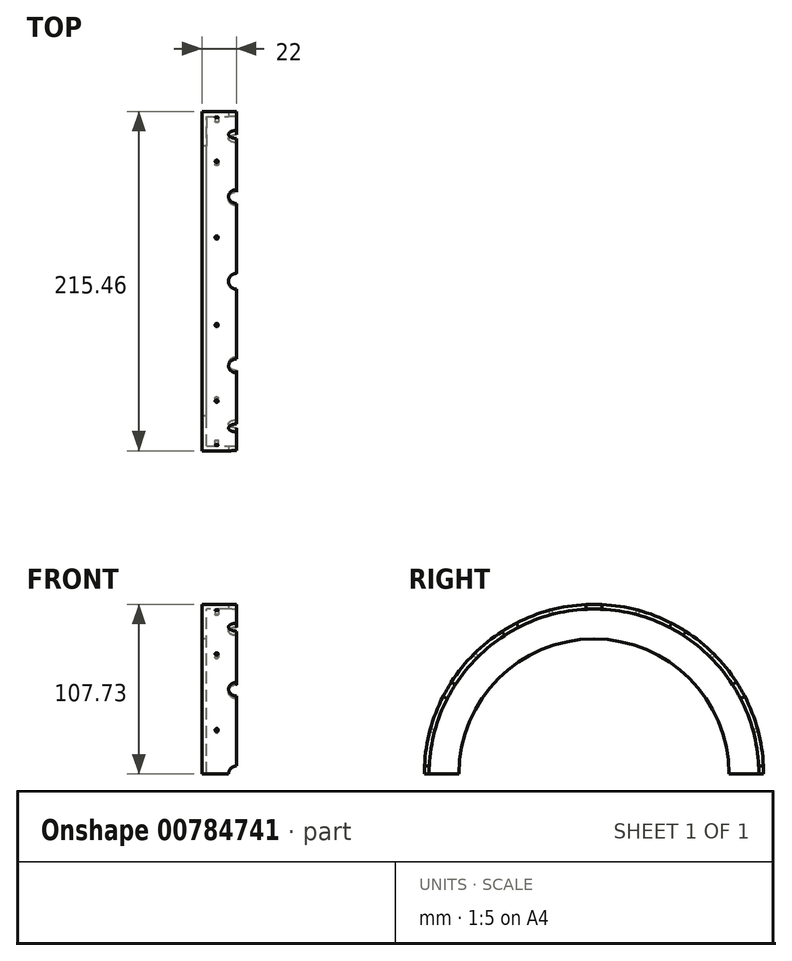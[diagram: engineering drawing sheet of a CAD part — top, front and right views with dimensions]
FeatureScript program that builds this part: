
annotation { "Feature Type Name" : "Feature", "Feature Type Description" : "" }
export const myFeature = defineFeature(function(context is Context, id is Id, definition is map)
    precondition{}
    {
        {
            var Q0;
            Q0=qCreatedBy(makeId("Top.planeOp"),FACE);
            var sketch = newSketch(context, id + "F0", { "sketchPlane" : qUnion([Q0])});
            skLineSegment(sketch, "E0", {"start": v(-37.45, 0) * mm, "end": v(31.85, 0) * mm, "construction": true});
            skLineSegment(sketch, "E1", {"start": v(-6.93, 104.73) * mm, "end": v(-6.93, 85.73) * mm});
            skLineSegment(sketch, "E2", {"start": v(-6.93, 85.73) * mm, "end": v(-9.93, 85.73) * mm});
            skLineSegment(sketch, "E3", {"start": v(-9.93, 85.73) * mm, "end": v(-9.93, 107.73) * mm});
            skLineSegment(sketch, "E4", {"start": v(-6.93, 104.73) * mm, "end": v(9.07, 104.73) * mm});
            skLineSegment(sketch, "E5", {"start": v(12.07, 107.73) * mm, "end": v(12.07, 104.73) * mm});
            skLineSegment(sketch, "E6", {"start": v(-9.93, 107.73) * mm, "end": v(12.07, 107.73) * mm});
            skLineSegment(sketch, "E7.trimOffspring", {"start": v(10.07, 104.73) * mm, "end": v(12.07, 104.73) * mm});
            skLineSegment(sketch, "E8", {"start": v(9.07, 104.73) * mm, "end": v(10.07, 104.73) * mm});
            skSolve(sketch);
        }
        {
            var Q0;
            Q0 = qSketchRegion(id + "F0", true);
            var Q1;
            Q1=sQuery(id+"F0.wireOp",EDGE,"E0");
            revolve(context, id + "F1", {"surfaceOperationType" : NewSurfaceOperationType.NEW, "entities" : qUnion([Q0]), "axis" : qUnion([Q1]), "revolveType" : RevolveType.ONE_DIRECTION, "angle" : 180 * degree});
        }
        {
            var Q0;
            Q0=qCreatedBy(makeId("Right.planeOp"),FACE);
            var sketch = newSketch(context, id + "F2", { "sketchPlane" : qUnion([Q0])});
            skLineSegment(sketch, "E9", {"start": v(0, 0) * mm, "end": v(61.84, 107.11) * mm, "construction": true});
            skLineSegment(sketch, "E10", {"start": v(0, 0) * mm, "end": v(0, 110.2) * mm, "construction": true});
            skLineSegment(sketch, "E11", {"start": v(0, 0) * mm, "end": v(-59.27, 102.65) * mm, "construction": true});
            skLineSegment(sketch, "E12", {"start": v(0, 0) * mm, "end": v(108.53, 62.66) * mm, "construction": true});
            skLineSegment(sketch, "E13", {"start": v(0, 0) * mm, "end": v(-111.98, 64.65) * mm, "construction": true});
            skLineSegment(sketch, "E14", {"start": v(0, 0) * mm, "end": v(-132.1, 0) * mm, "construction": true});
            skLineSegment(sketch, "E15", {"start": v(0, 0) * mm, "end": v(126.53, 0) * mm, "construction": true});
            skPoint(sketch, "E16", {"position": v(-59.27, 102.65) * mm});
            skPoint(sketch, "E17", {"position": v(-111.98, 64.65) * mm});
            skPoint(sketch, "E18", {"position": v(-132.1, 0) * mm});
            skPoint(sketch, "E19", {"position": v(0, 110.2) * mm});
            skPoint(sketch, "E20", {"position": v(61.84, 107.11) * mm});
            skPoint(sketch, "E21", {"position": v(108.53, 62.66) * mm});
            skPoint(sketch, "E22", {"position": v(126.53, 0) * mm});
            skLineSegment(sketch, "E23", {"start": v(0, 0) * mm, "end": v(-120.74, 32.35) * mm, "construction": true});
            skLineSegment(sketch, "E24.MirrorCS", {"start": v(0, 0) * mm, "end": v(-88.39, 88.39) * mm, "construction": true});
            skLineSegment(sketch, "E25.MirrorCS", {"start": v(0, 0) * mm, "end": v(-32.35, 120.74) * mm, "construction": true});
            skLineSegment(sketch, "E26.MirrorCS", {"start": v(0, 0) * mm, "end": v(32.35, 120.74) * mm, "construction": true});
            skLineSegment(sketch, "E27.MirrorCS", {"start": v(0, 0) * mm, "end": v(88.39, 88.39) * mm, "construction": true});
            skLineSegment(sketch, "E28.MirrorCS", {"start": v(0, 0) * mm, "end": v(120.74, 32.35) * mm, "construction": true});
            skSolve(sketch);
        }
        {
            var Q0;
            Q0=qCreatedBy(makeId("Front.planeOp"),FACE);
            var Q1;
            Q1=sQuery(id+"F2.wireOp",EDGE,"E13");
            cPlane(context, id + "F3", {"entities" : qUnion([Q0, Q1]), "cplaneType" : CPlaneType.LINE_ANGLE, "offset" : 25 * mm, "angle" : 0 * degree, "width" : 150 * mm, "height" : 150 * mm});
        }
        {
            var Q0;
            Q0=qCreatedBy(id+"F3.planeOp",FACE);
            var sketch = newSketch(context, id + "F4", { "sketchPlane" : qUnion([Q0])});
            skArc(sketch, "E29", {"start": v(12.07, -113.43) * mm, "mid": v(17.27, -105.94) * mm, "end": v(12.07, -98.44) * mm});
            skLineSegment(sketch, "E30", {"start": v(12.07, -113.43) * mm, "end": v(12.07, -98.44) * mm});
            skSolve(sketch);
        }
        {
            var Q0;
            Q0 = qSketchRegion(id + "F4", true);
            var Q1;
            Q1=sQuery(id+"F4.wireOp",EDGE,"E30");
            revolve(context, id + "F5", {"operationType" : NewBodyOperationType.REMOVE, "surfaceOperationType" : NewSurfaceOperationType.NEW, "entities" : qUnion([Q0]), "axis" : qUnion([Q1]), "revolveType" : RevolveType.FULL, "oppositeDirection" : true});
        }
        {
            var Q0;
            Q0=sQuery(id+"F2.wireOp",EDGE,"E11");
            cPlane(context, id + "F6", {"entities" : qUnion([Q0]), "cplaneType" : CPlaneType.LINE_ANGLE, "offset" : 25 * mm, "angle" : 90 * degree, "width" : 150 * mm, "height" : 150 * mm});
        }
        {
            var Q0;
            Q0=qCreatedBy(id+"F6.planeOp",FACE);
            var sketch = newSketch(context, id + "F7", { "sketchPlane" : qUnion([Q0])});
            skArc(sketch, "E31", {"start": v(-12.1, 98.77) * mm, "mid": v(-6.9, 106.26) * mm, "end": v(-12.1, 113.76) * mm});
            skLineSegment(sketch, "E32", {"start": v(-12.1, 98.77) * mm, "end": v(-12.1, 113.76) * mm});
            skSolve(sketch);
        }
        {
            var Q0;
            Q0 = qSketchRegion(id + "F7", true);
            var Q1;
            Q1=sQuery(id+"F7.wireOp",EDGE,"E32");
            revolve(context, id + "F8", {"operationType" : NewBodyOperationType.REMOVE, "surfaceOperationType" : NewSurfaceOperationType.NEW, "entities" : qUnion([Q0]), "axis" : qUnion([Q1]), "revolveType" : RevolveType.FULL, "oppositeDirection" : true});
        }
        {
            var Q0;
            Q0=sQuery(id+"F2.wireOp",EDGE,"E10");
            cPlane(context, id + "F9", {"entities" : qUnion([Q0]), "cplaneType" : CPlaneType.LINE_ANGLE, "offset" : 25 * mm, "angle" : 90 * degree, "width" : 150 * mm, "height" : 150 * mm});
        }
        {
            var Q0;
            Q0=qCreatedBy(id+"F9.planeOp",FACE);
            var sketch = newSketch(context, id + "F10", { "sketchPlane" : qUnion([Q0])});
            skArc(sketch, "E33", {"start": v(-12.07, 98.66) * mm, "mid": v(-6.87, 106.16) * mm, "end": v(-12.07, 113.65) * mm});
            skLineSegment(sketch, "E34", {"start": v(-12.07, 98.66) * mm, "end": v(-12.07, 113.65) * mm});
            skSolve(sketch);
        }
        {
            var Q0;
            Q0 = qSketchRegion(id + "F10", true);
            var Q1;
            Q1=sQuery(id+"F10.wireOp",EDGE,"E34");
            revolve(context, id + "F11", {"operationType" : NewBodyOperationType.REMOVE, "surfaceOperationType" : NewSurfaceOperationType.NEW, "entities" : qUnion([Q0]), "axis" : qUnion([Q1]), "revolveType" : RevolveType.FULL, "oppositeDirection" : true});
        }
        {
            var Q0;
            Q0=sQuery(id+"F2.wireOp",EDGE,"E9");
            cPlane(context, id + "F12", {"entities" : qUnion([Q0]), "cplaneType" : CPlaneType.LINE_ANGLE, "offset" : 25 * mm, "angle" : 90 * degree, "width" : 150 * mm, "height" : 150 * mm});
        }
        {
            var Q0;
            Q0=qCreatedBy(id+"F12.planeOp",FACE);
            var sketch = newSketch(context, id + "F13", { "sketchPlane" : qUnion([Q0])});
            skArc(sketch, "E35", {"start": v(-12.07, 98.61) * mm, "mid": v(-6.87, 106.1) * mm, "end": v(-12.07, 113.6) * mm});
            skLineSegment(sketch, "E36", {"start": v(-12.07, 98.61) * mm, "end": v(-12.07, 113.6) * mm});
            skSolve(sketch);
        }
        {
            var Q0;
            Q0 = qSketchRegion(id + "F13", true);
            var Q1;
            Q1=sQuery(id+"F13.wireOp",EDGE,"E36");
            revolve(context, id + "F14", {"operationType" : NewBodyOperationType.REMOVE, "surfaceOperationType" : NewSurfaceOperationType.NEW, "entities" : qUnion([Q0]), "axis" : qUnion([Q1]), "revolveType" : RevolveType.FULL, "oppositeDirection" : true});
        }
        {
            var Q0;
            Q0=sQuery(id+"F2.wireOp",EDGE,"E12");
            cPlane(context, id + "F15", {"entities" : qUnion([Q0]), "cplaneType" : CPlaneType.LINE_ANGLE, "offset" : 25 * mm, "angle" : 0 * degree, "width" : 150 * mm, "height" : 150 * mm});
        }
        {
            var Q0;
            Q0=qCreatedBy(id+"F15.planeOp",FACE);
            var sketch = newSketch(context, id + "F16", { "sketchPlane" : qUnion([Q0])});
            skArc(sketch, "E37", {"start": v(12.07, 98.66) * mm, "mid": v(17.27, 106.16) * mm, "end": v(12.07, 113.65) * mm});
            skLineSegment(sketch, "E38", {"start": v(12.07, 98.66) * mm, "end": v(12.07, 113.65) * mm});
            skSolve(sketch);
        }
        {
            var Q0;
            Q0 = qSketchRegion(id + "F16", true);
            var Q1;
            Q1=sQuery(id+"F16.wireOp",EDGE,"E38");
            revolve(context, id + "F17", {"operationType" : NewBodyOperationType.REMOVE, "surfaceOperationType" : NewSurfaceOperationType.NEW, "entities" : qUnion([Q0]), "axis" : qUnion([Q1]), "revolveType" : RevolveType.FULL, "oppositeDirection" : true});
        }
        {
            var Q0;
            Q0=sQuery(id+"F2.wireOp",EDGE,"E23");
            cPlane(context, id + "F18", {"entities" : qUnion([Q0]), "cplaneType" : CPlaneType.LINE_ANGLE, "offset" : 25 * mm, "angle" : 0 * degree, "width" : 150 * mm, "height" : 150 * mm});
        }
        {
            var Q0;
            Q0=sQuery(id+"F2.wireOp",EDGE,"E24.MirrorCS");
            cPlane(context, id + "F19", {"entities" : qUnion([Q0]), "cplaneType" : CPlaneType.LINE_ANGLE, "offset" : 25 * mm, "angle" : 0 * degree, "width" : 150 * mm, "height" : 150 * mm});
        }
        {
            var Q0;
            Q0=sQuery(id+"F2.wireOp",EDGE,"E25.MirrorCS");
            cPlane(context, id + "F20", {"entities" : qUnion([Q0]), "cplaneType" : CPlaneType.LINE_ANGLE, "offset" : 25 * mm, "angle" : 90 * degree, "width" : 150 * mm, "height" : 150 * mm});
        }
        {
            var Q0;
            Q0=sQuery(id+"F2.wireOp",EDGE,"E26.MirrorCS");
            cPlane(context, id + "F21", {"entities" : qUnion([Q0]), "cplaneType" : CPlaneType.LINE_ANGLE, "offset" : 25 * mm, "angle" : 90 * degree, "width" : 150 * mm, "height" : 150 * mm});
        }
        {
            var Q0;
            Q0=sQuery(id+"F2.wireOp",EDGE,"E27.MirrorCS");
            cPlane(context, id + "F22", {"entities" : qUnion([Q0]), "cplaneType" : CPlaneType.LINE_ANGLE, "offset" : 25 * mm, "angle" : 0 * degree, "width" : 150 * mm, "height" : 150 * mm});
        }
        {
            var Q0;
            Q0=sQuery(id+"F2.wireOp",EDGE,"E28.MirrorCS");
            cPlane(context, id + "F23", {"entities" : qUnion([Q0]), "cplaneType" : CPlaneType.LINE_ANGLE, "offset" : 25 * mm, "angle" : 0 * degree, "width" : 150 * mm, "height" : 150 * mm});
        }
        {
            var Q0;
            Q0=qCreatedBy(id+"F18.planeOp",FACE);
            var sketch = newSketch(context, id + "F24", { "sketchPlane" : qUnion([Q0])});
            skLineSegment(sketch, "E39.bottom", {"start": v(-1.5, 110.33) * mm, "end": v(-0.5, 110.33) * mm});
            skLineSegment(sketch, "E39.top", {"start": v(-1.5, 102.33) * mm, "end": v(-0.5, 102.33) * mm});
            skLineSegment(sketch, "E39.left", {"start": v(-1.5, 110.33) * mm, "end": v(-1.5, 102.33) * mm});
            skLineSegment(sketch, "E39.right", {"start": v(-0.5, 110.33) * mm, "end": v(-0.5, 102.33) * mm});
            skSolve(sketch);
        }
        {
            var Q0;
            Q0 = qSketchRegion(id + "F24", true);
            var Q1;
            Q1=sQuery(id+"F24.wireOp",EDGE,"E39.right");
            revolve(context, id + "F25", {"operationType" : NewBodyOperationType.REMOVE, "surfaceOperationType" : NewSurfaceOperationType.NEW, "entities" : qUnion([Q0]), "axis" : qUnion([Q1]), "revolveType" : RevolveType.FULL, "oppositeDirection" : true});
        }
        {
            var Q0;
            Q0=qCreatedBy(id+"F19.planeOp",FACE);
            var sketch = newSketch(context, id + "F26", { "sketchPlane" : qUnion([Q0])});
            skLineSegment(sketch, "E40.bottom", {"start": v(-1.5, 111.6) * mm, "end": v(-0.5, 111.6) * mm});
            skLineSegment(sketch, "E40.top", {"start": v(-1.5, 103.6) * mm, "end": v(-0.5, 103.6) * mm});
            skLineSegment(sketch, "E40.left", {"start": v(-1.5, 111.6) * mm, "end": v(-1.5, 103.6) * mm});
            skLineSegment(sketch, "E40.right", {"start": v(-0.5, 111.6) * mm, "end": v(-0.5, 103.6) * mm});
            skSolve(sketch);
        }
        {
            var Q0;
            Q0 = qSketchRegion(id + "F26", true);
            var Q1;
            Q1=sQuery(id+"F26.wireOp",EDGE,"E40.right");
            revolve(context, id + "F27", {"operationType" : NewBodyOperationType.REMOVE, "surfaceOperationType" : NewSurfaceOperationType.NEW, "entities" : qUnion([Q0]), "axis" : qUnion([Q1]), "revolveType" : RevolveType.FULL, "oppositeDirection" : true});
        }
        {
            var Q0;
            Q0=qCreatedBy(id+"F20.planeOp",FACE);
            var sketch = newSketch(context, id + "F28", { "sketchPlane" : qUnion([Q0])});
            skLineSegment(sketch, "E41.bottom", {"start": v(0.5, 111.69) * mm, "end": v(1.5, 111.69) * mm});
            skLineSegment(sketch, "E41.top", {"start": v(0.5, 103.69) * mm, "end": v(1.5, 103.69) * mm});
            skLineSegment(sketch, "E41.left", {"start": v(0.5, 111.69) * mm, "end": v(0.5, 103.69) * mm});
            skLineSegment(sketch, "E41.right", {"start": v(1.5, 111.69) * mm, "end": v(1.5, 103.69) * mm});
            skSolve(sketch);
        }
        {
            var Q0;
            Q0 = qSketchRegion(id + "F28", true);
            var Q1;
            Q1=sQuery(id+"F28.wireOp",EDGE,"E41.left");
            revolve(context, id + "F29", {"operationType" : NewBodyOperationType.REMOVE, "surfaceOperationType" : NewSurfaceOperationType.NEW, "entities" : qUnion([Q0]), "axis" : qUnion([Q1]), "revolveType" : RevolveType.FULL, "oppositeDirection" : true});
        }
        {
            var Q0;
            Q0=qCreatedBy(id+"F21.planeOp",FACE);
            var sketch = newSketch(context, id + "F30", { "sketchPlane" : qUnion([Q0])});
            skLineSegment(sketch, "E42.bottom", {"start": v(0.5, 112.04) * mm, "end": v(1.5, 112.04) * mm});
            skLineSegment(sketch, "E42.top", {"start": v(0.5, 104.04) * mm, "end": v(1.5, 104.04) * mm});
            skLineSegment(sketch, "E42.left", {"start": v(0.5, 112.04) * mm, "end": v(0.5, 104.04) * mm});
            skLineSegment(sketch, "E42.right", {"start": v(1.5, 112.04) * mm, "end": v(1.5, 104.04) * mm});
            skSolve(sketch);
        }
        {
            var Q0;
            Q0 = qSketchRegion(id + "F30", true);
            var Q1;
            Q1=sQuery(id+"F30.wireOp",EDGE,"E42.left");
            revolve(context, id + "F31", {"operationType" : NewBodyOperationType.REMOVE, "surfaceOperationType" : NewSurfaceOperationType.NEW, "entities" : qUnion([Q0]), "axis" : qUnion([Q1]), "revolveType" : RevolveType.FULL, "oppositeDirection" : true});
        }
        {
            var Q0;
            Q0=qCreatedBy(id+"F22.planeOp",FACE);
            var sketch = newSketch(context, id + "F32", { "sketchPlane" : qUnion([Q0])});
            skLineSegment(sketch, "E43.bottom", {"start": v(-1.5, 112) * mm, "end": v(-0.5, 112) * mm});
            skLineSegment(sketch, "E43.top", {"start": v(-1.5, 104) * mm, "end": v(-0.5, 104) * mm});
            skLineSegment(sketch, "E43.left", {"start": v(-1.5, 112) * mm, "end": v(-1.5, 104) * mm});
            skLineSegment(sketch, "E43.right", {"start": v(-0.5, 112) * mm, "end": v(-0.5, 104) * mm});
            skSolve(sketch);
        }
        {
            var Q0;
            Q0 = qSketchRegion(id + "F32", true);
            var Q1;
            Q1=sQuery(id+"F32.wireOp",EDGE,"E43.right");
            revolve(context, id + "F33", {"operationType" : NewBodyOperationType.REMOVE, "surfaceOperationType" : NewSurfaceOperationType.NEW, "entities" : qUnion([Q0]), "axis" : qUnion([Q1]), "revolveType" : RevolveType.FULL, "oppositeDirection" : true});
        }
        {
            var Q0;
            Q0=qCreatedBy(id+"F23.planeOp",FACE);
            var sketch = newSketch(context, id + "F34", { "sketchPlane" : qUnion([Q0])});
            skLineSegment(sketch, "E44.bottom", {"start": v(-1.5, 110.24) * mm, "end": v(-0.5, 110.24) * mm});
            skLineSegment(sketch, "E44.top", {"start": v(-1.5, 102.24) * mm, "end": v(-0.5, 102.24) * mm});
            skLineSegment(sketch, "E44.left", {"start": v(-1.5, 110.24) * mm, "end": v(-1.5, 102.24) * mm});
            skLineSegment(sketch, "E44.right", {"start": v(-0.5, 110.24) * mm, "end": v(-0.5, 102.24) * mm});
            skSolve(sketch);
        }
        {
            var Q0;
            Q0 = qSketchRegion(id + "F34", true);
            var Q1;
            Q1=sQuery(id+"F34.wireOp",EDGE,"E44.right");
            revolve(context, id + "F35", {"operationType" : NewBodyOperationType.REMOVE, "surfaceOperationType" : NewSurfaceOperationType.NEW, "entities" : qUnion([Q0]), "axis" : qUnion([Q1]), "revolveType" : RevolveType.FULL, "oppositeDirection" : true});
        }
        {
            var Q0;
            Q0=qCreatedBy(makeId("Top.planeOp"),FACE);
            var sketch = newSketch(context, id + "F36", { "sketchPlane" : qUnion([Q0])});
            skArc(sketch, "E45", {"start": v(12.07, 98.74) * mm, "mid": v(17.27, 106.24) * mm, "end": v(12.07, 113.73) * mm});
            skLineSegment(sketch, "E46", {"start": v(12.07, 98.74) * mm, "end": v(12.07, 113.73) * mm});
            skLineSegment(sketch, "E47.MirrorCS", {"start": v(12.07, -98.74) * mm, "end": v(12.07, -113.73) * mm});
            skArc(sketch, "E48.MirrorCS", {"start": v(12.07, -98.74) * mm, "mid": v(17.27, -106.24) * mm, "end": v(12.07, -113.73) * mm});
            skSolve(sketch);
        }
        {
            var Q0;
            Q0 = qSketchRegion(id + "F36", true);
            var Q1;
            Q1=sQuery(id+"F36.wireOp",EDGE,"E46");
            revolve(context, id + "F37", {"operationType" : NewBodyOperationType.REMOVE, "surfaceOperationType" : NewSurfaceOperationType.NEW, "entities" : qUnion([Q0]), "axis" : qUnion([Q1]), "revolveType" : RevolveType.ONE_DIRECTION, "oppositeDirection" : true, "angle" : 180 * degree});
        }
    });
